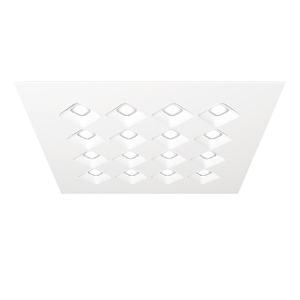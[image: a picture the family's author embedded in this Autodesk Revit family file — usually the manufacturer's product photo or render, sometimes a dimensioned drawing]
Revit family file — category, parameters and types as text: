
# Revit family: 3f_filippi_-_3f_diagon_soft_ugr_3f_filippi_-_23831_-_3f_diagon_25w-830_ep_soft_ugr_621x621
name_source: partatom
category: Lighting Fixtures
units: mm (PartAtom-declared; Revit-internal decimal feet)

## family parameters
Cut with Voids When Loaded = No
Host = Face
Light Source = No
Part Type = Normal
Room Calculation Point = No
Round Connector Dimension = Use Diameter
Shared = No

## types (1)
- 3F Filippi - 3F Dìagon Soft UGR (1 x LED, 3495 lm, 29 W, 3000 K)
    Apparent Load = 29 VA
    Approval mark = ENEC
    CIE Flux Codes = 59 92 100 100 100
    Color Rendering = 80
    Color Temperature = 3000 K
    Control Gear = Electronic ballast
    Default Elevation = 1800 mm
    Description = ILLUMINOTECHNICAL
Luminous efficiency 100% (DLOR 100%, ULOR 0%).
Initial luminous flux of the luminaire 3495 lm.
Emergency luminaire luminous flux BLF 19.8%.
Direct symmetric distribution.
Installation Interdistance Transv.D = 1.23 x hu - Long.D = 1.23 x hu.
Average luminance <3000 cd/m² for radial angles >65°.
Tabular UGR (CIE 117 - 4H-8H; S=0.25H; 70/50/20): RUG 18.6 - 18.5.
Beam angle: 102° - 101°.
Luminous efficacy 121 lm/W.
Lifetime (L95/B10): 30000 h. (tq+25°C)
Lifetime (L90/B10): 50000 h. (tq+25°C)
Lifetime (L80/B10): 80000 h. (tq+25°C)
Lifetime (L75/B10): 100000 h. (tq+25°C)
Sudden decreased luminous flux after 50000 hours: 0% (C0).
Photobiological safety in compliance with IEC/TR 62778: RG0 risk exempt, (IEC 62471).
In compliance with IEC/EN 62722-2-1 - IEC/EN 62717 standards.

SOURCE
Squared LED module 25W/830.
Energy efficiency class (UE 2019/2020 - UE 2019/2015): C.
CIE 13.3 Colour rendering index: CRI >80 (R9 <50%).
IES TM-30 Fidelity Index: Rf = 84 Rg = 95.
CCT nominal colour temperature 3000 K.
Colour initial tolerance (MacAdam): SDCM 3.

MECHANICAL
Housing in hot-galvanised steel, painted in white polyester.
Honeycombed diagonal screen in white anti-glare polycarbonate.
Opal methacrylate (PMMA) rhomboid lenses with differentiated, engraved and prismatic surfaces for diffused, soft lighting and excellent visual comfort.
Luminaire with limited surface temperature. - D - (EN 60598-2-24)
Dimensions: 621x621 mm, height 30 mm. Weight 4.7 kg.
IP43 protection degree for exposed part, IP20 for recessed part.
Mechanical strength to impacts IK06 (1 joule).
Glow-wire test resistance 650°C.

ELECTRICAL
Halogen Free electronic wiring 230V-50/60Hz, power factor 0.90, THD <25%, constant output current, class I, 1 driver.
Power of the luminaire 29 W.
CE - IEC 60598-1 - EN 60598-1.
EP maintained emergency wiring on board, 1h duration, 24h recharge; compliant with EN 60598-2-22, excluding high risk areas.
SAFE FLICKER: PstLM=<1 and SVM=<0.4 (IEC TR 61547-1 and IEC TR 63158), to ensure a more comfortable and safe light.
Ambient temperature from +5°C to +25°C.
Temperature class T6 max 85°C.
Quick connection.
Relative humidity UR: <85%.

INSTALLATION
Lay-in recessed fitting.
Height only 30 mm.
Installation on false ceilings with recessed dimensions greater than 596x596 standard size.
Installation after mounting the false ceiling, resting on the exposed structure, minimum void of 140 mm from the lower edge of the structure.
Simultaneous installation with the false ceiling, minimum void of 60 mm from the lower edge of the structure.
All accessories dedicated to this product are available on the Catalog and on our website www.3F-Filippi.com.

APPLICATIONS
Environments: staterooms, with VDTs, offices.
Environments with exacting visual tasks, where diffused soft light for optimum visual comfort is required.

WARNING
Luminaire designed for disposal/recycling at end-of-life.
Replaceable (LED only) light source by a professional. Replaceable control gear by a professional.
    Height = 0 mm  [stored 0 ft]
    Lamp = 1 x LED
    Lamp Light Flux = 3495 lm
    Lamp Power = 29 W
    Lamp count = 1
    Length = 621 mm
    Lifetime = 50000 h
    Luminous efficacy = 121 lm/W
    Manufacturer = 3F Filippi
    ModVariant = No
    Model = 3F Filippi - 23831 - 3F Diagon 25W-830 EP SOFT UGR 621x621
    Mounting Place = Ceiling
    Mounting Type = Recessed
    Number of Poles = 1
    OnlyDefault = Yes
    Power Factor = 1
    Product Name = 3F Filippi - 3F Dìagon Soft UGR
    Product group = recessed luminaire
    ProductGroupID = 4
    Protection Class = Protection class I
    Protection Degree = IP 20
    RLX_Detail_Level = 1
    RLX_Emergency_Light_Flux = 0 lm
    RLX_Emergency_Type = 0
    RLX_Emergency_Type_DB = No
    RlxData = <blob elided: 84609 chars, md5=453dea30>
    Socket = socket
    Standby Power = 0 W
    System Light Flux = 3495 lm
    System Power = 29 W
    Type Comments = Product without accessories
    Type Image = 3ffilippi_3f_diagon_soft_ugr.jpg
    URL = http://relux.com
    VarID = ---
    Voltage = 0 V
    Weight = 0.00 kg
    Width = 621 mm

note: [stored X ft] marks values corroborated as IEEE doubles in the binary element streams (Revit-internal decimal feet)

## geometry (parser evidence)
native form markers: Blend x4, Sweep x12
no freeform markers — native parametric forms only
